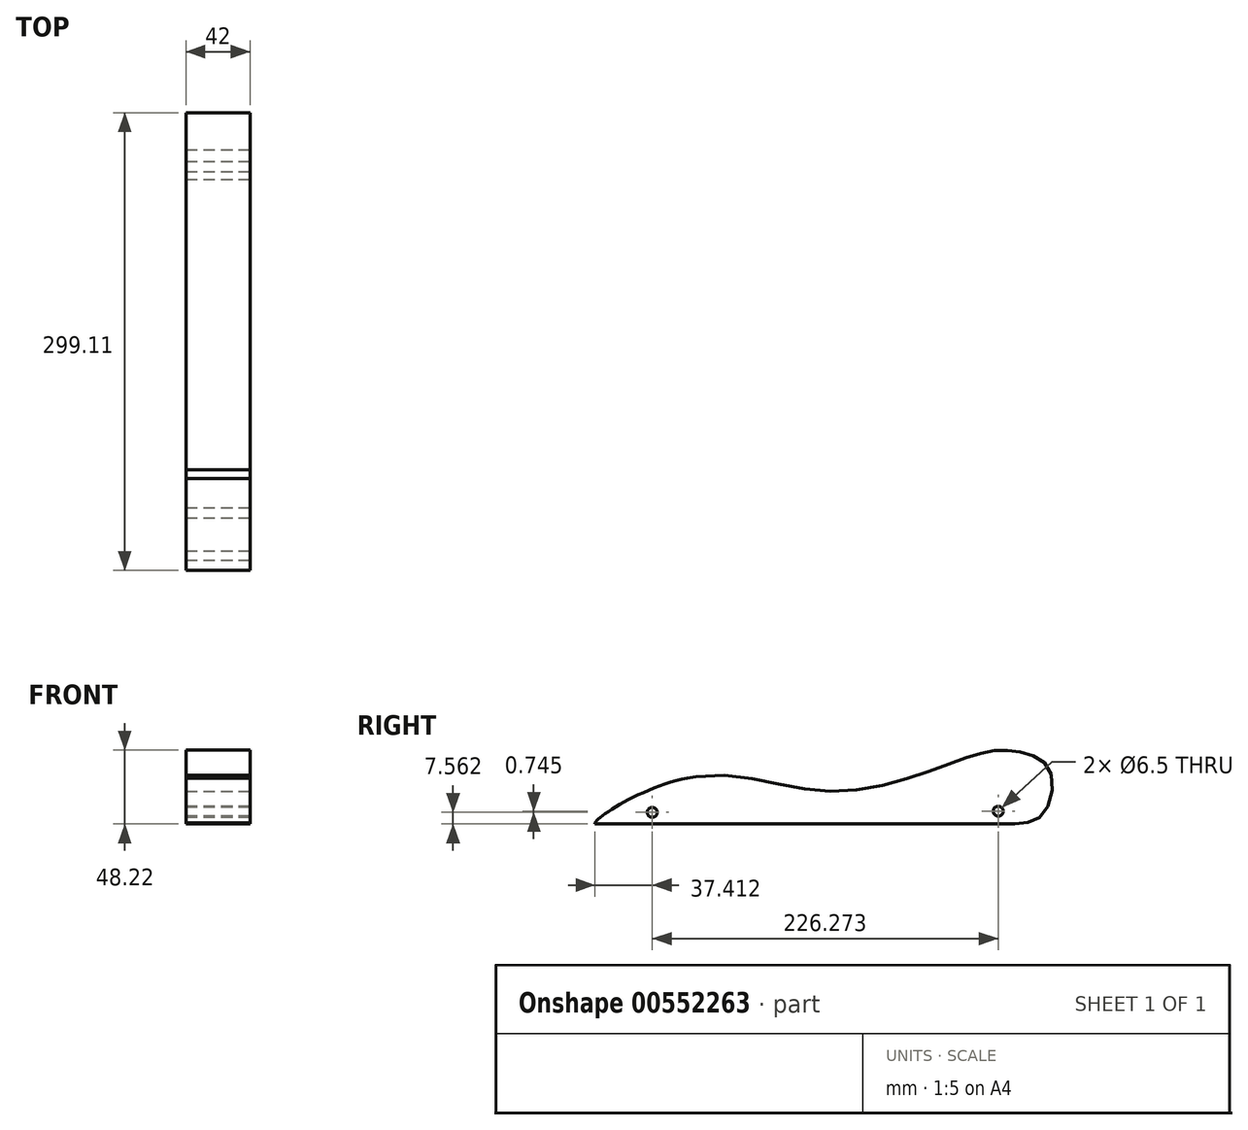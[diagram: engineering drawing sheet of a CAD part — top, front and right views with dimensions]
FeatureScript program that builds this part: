
annotation { "Feature Type Name" : "Feature", "Feature Type Description" : "" }
export const myFeature = defineFeature(function(context is Context, id is Id, definition is map)
    precondition{}
    {
        {
            var Q0;
            Q0=qCreatedBy(makeId("Right.planeOp"),FACE);
            var sketch = newSketch(context, id + "F0", { "sketchPlane" : qUnion([Q0])});
            skLineSegment(sketch, "E0.bottom", {"start": v(149.97, -35) * mm, "end": v(-149.97, -35) * mm});
            skLineSegment(sketch, "E0.left", {"start": v(149.97, -35) * mm, "end": v(149.97, 35) * mm});
            skLineSegment(sketch, "E0.right", {"start": v(-149.97, -35) * mm, "end": v(-149.97, -15) * mm});
            skPoint(sketch, "E0.middle", {"position": v(0, 0) * mm});
            skLineSegment(sketch, "E1", {"start": v(149.97, 35) * mm, "end": v(-149.97, -15) * mm});
            skPoint(sketch, "E0.top.end.orphan", {"position": v(-149.97, 35) * mm});
            skCircle(sketch, "E2", {"center": v(-112.56, -27.44) * mm, "radius": 3.25 * mm});
            skCircle(sketch, "E3", {"center": v(113.71, -26.7) * mm, "radius": 3.25 * mm});
            skFitSpline(sketch, "E4", {"points": [v(-149.97, -35) * mm, v(-89.75, -4.96) * mm, v(2.55, -13.7) * mm, v(76.63, 2.35) * mm, v(109.4, 12.64) * mm, v(130.14, 11.55) * mm, v(147.42, 0) * mm, v(143.14, -28.37) * mm, v(124.67, -35) * mm, v(105.5, -35) * mm, v(80.8, -35) * mm, v(-137.64, -35) * mm, v(-143.7, -35) * mm, v(-149.97, -35) * mm]});
            skSolve(sketch);
        }
        {
            var Q0;
            Q0=makeQuery(id+"F0.imprint","IMPRINT",FACE,{"disambiguationData":[TD([[makeQuery(id+"F0.imprint","IMPRINT",EDGE,{"derivedFrom":sQuery(id+"F0.wireOp",EDGE,"E0.bottom")}),-1.0]])]});
            extrude(context, id + "F1", {"entities" : qUnion([Q0]), "endBound" : BoundingType.SYMMETRIC, "depth" : 42 * mm, "offsetDistance" : 25 * mm});
        }
    });
